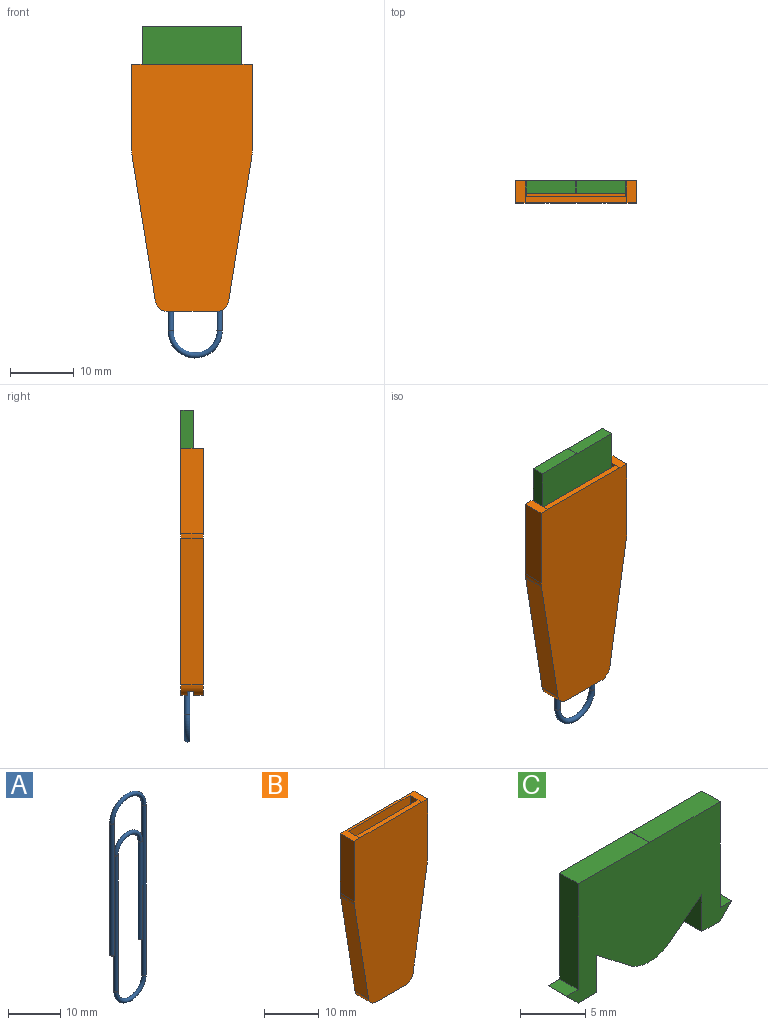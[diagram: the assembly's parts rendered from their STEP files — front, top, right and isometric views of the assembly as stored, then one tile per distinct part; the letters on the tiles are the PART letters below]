
ASSEMBLY  parts=3 mates=2
PART A: 9 faces, bbox 10.3x0.9x49.8 mm
  f0: plane 0.87x0.87mm, normal (0,0,-1), area 0.6mm2, adj f2
  f1: plane 0.87x0.87mm, normal (0,0,-1), area 0.6mm2, adj f8
  f2: cylinder r=0.43mm len=23mm, axis (0,0,1), area 62.9mm2, adj f0,f3
  f3: torus R=3.31mm, axis (0,-1,0), area 28.4mm2, adj f2,f4
  f4: cylinder r=0.43mm len=32mm, axis (0,0,-1), area 87.5mm2, adj f3,f5
  f5: torus R=3.81mm, axis (0,-1,0), area 32.7mm2, adj f4,f6
  f6: cylinder r=0.43mm len=40mm, axis (0,0,1), area 109.3mm2, adj f5,f7
  f7: torus R=4.33mm, axis (0,-1,0), area 37.2mm2, adj f6,f8
  f8: cylinder r=0.43mm len=31mm, axis (0,0,-1), area 84.7mm2, adj f1,f7
PART B: 29 faces, bbox 19x3.5x38.7 mm
  f0: plane 7.55x1.5mm, normal (0,0,-1), area 11.3mm2, adj f15,f16,f25,f26
  f1: plane 15.45x2mm, normal (0,0,1), area 20.4mm2, adj f2,f3,f8,f12,f15,f17,f20,f22
  f2: plane 2x1.51mm, normal (-0.71,0,0.71), area 4.3mm2, adj f1,f5,f20,f22
  f3: plane 2x1.51mm, normal (0.71,0,0.71), area 4.3mm2, adj f1,f6,f20,f22
  f4: plane 9.97x2mm, normal (-1,0,0), area 19.9mm2, adj f5,f11,f20,f22
  f5: plane 2x1.26mm, normal (0,0,-1), area 2.5mm2, adj f2,f4,f20,f22
  f6: plane 2x1.26mm, normal (0,0,-1), area 2.5mm2, adj f3,f7,f20,f22
  f7: plane 9.97x2mm, normal (1,0,0), area 19.9mm2, adj f6,f13,f20,f22
  f8: plane 26.58x1mm, normal (-1,0,0), area 26.6mm2, adj f1,f15,f17,f26
  f9: plane 7.55x1mm, normal (0,0,-1), area 7.5mm2, adj f17,f18,f25,f26
  f10: plane 13.33x3.5mm, normal (1,0,0), area 46.6mm2, adj f11,f16,f18,f27
  f11: plane 3.5x1.51mm, normal (0,0,1), area 5.3mm2, adj f4,f10,f16,f18,f19,f21
  f12: plane 26.58x1mm, normal (1,0,0), area 26.6mm2, adj f1,f15,f17,f25
  f13: plane 3.5x1.51mm, normal (0,0,1), area 5.3mm2, adj f7,f14,f16,f18,f19,f21
  f14: plane 13.33x3.5mm, normal (-1,0,0), area 46.6mm2, adj f13,f16,f18,f28
  f15: plane 27.25x10.54mm, normal (0,1,0), area 286.6mm2, adj f0,f1,f8,f12,f25,f26
  f16: plane 38.72x18.96mm, normal (0,-1,0), area 632.9mm2, adj f0,f10,f11,f13,f14,f19,f23,f24
  f17: plane 27.25x10.54mm, normal (0,-1,0), area 286.6mm2, adj f1,f8,f9,f12,f25,f26
  f18: plane 38.72x18.96mm, normal (0,1,0), area 632.9mm2, adj f9,f10,f11,f13,f14,f21,f23,f24
  f19: plane 15.95x1mm, normal (0,0,1), area 15.9mm2, adj f11,f13,f16,f20
  f20: plane 18.46x11.47mm, normal (0,1,0), area 184.4mm2, adj f1,f2,f3,f4,f5,f6,f7,f19
  f21: plane 15.95x0.5mm, normal (0,0,1), area 8mm2, adj f11,f13,f18,f22
  f22: plane 18.46x11.47mm, normal (0,-1,0), area 184.4mm2, adj f1,f2,f3,f4,f5,f6,f7,f21
  f23: plane 22.92x3.67mm, normal (-0.99,0,-0.16), area 81.3mm2, adj f16,f18,f25,f28
  f24: plane 22.92x3.67mm, normal (0.99,0,-0.16), area 81.3mm2, adj f16,f18,f26,f27
  f25: cylinder r=2mm len=3.5mm, axis (0,1,0), area 8.2mm2, adj f0,f9,f12,f15,f16,f17,f18,f23
  f26: cylinder r=2mm len=3.5mm, axis (0,1,0), area 8.2mm2, adj f0,f8,f9,f15,f16,f17,f18,f24
  f27: cylinder r=5mm len=3.5mm, axis (0,-1,0), area 2.8mm2, adj f10,f16,f18,f24
  f28: cylinder r=5mm len=3.5mm, axis (0,1,0), area 2.8mm2, adj f14,f16,f18,f23
PART C: 21 faces, bbox 18x2x11.2 mm
  f0: cylinder r=3.5mm len=7mm, axis (0,1,0), area 35.3mm2, adj f1,f2,f18,f19,f20
  f1: plane 17.96x11.22mm, normal (0,-1,0), area 158.8mm2, adj f0,f4,f5,f6,f7,f8,f9,f10
  f2: plane 7x7mm, normal (0,1,0), area 38.5mm2, adj f0
  f3: cylinder r=5.72mm len=11.45mm, axis (0,1,0), area 27mm2, adj f11,f12,f17,f19
  f4: plane 7.69x2mm, normal (0,0,1), area 15.4mm2, adj f1,f5,f16,f17
  f5: cylinder r=7.72mm len=2mm, axis (0,1,0), area 0.1mm2, adj f1,f4,f6,f17
  f6: plane 7.72x2mm, normal (0,0,1), area 15.4mm2, adj f1,f5,f7,f17
  f7: plane 9.97x2mm, normal (-1,0,0), area 19.9mm2, adj f1,f6,f8,f17
  f8: plane 2x1.26mm, normal (0,0,1), area 2.5mm2, adj f1,f7,f9,f17
  f9: plane 2x1.26mm, normal (-0.71,0,-0.71), area 3.6mm2, adj f1,f8,f10,f17
  f10: plane 2x2mm, normal (0,0,-1), area 4mm2, adj f1,f9,f11,f17
  f11: plane 3.5x2mm, normal (1,0,0), area 7mm2, adj f1,f3,f10,f17,f18
  f12: plane 3.45x2mm, normal (-1,0,0), area 6.9mm2, adj f1,f3,f13,f17,f20
  f13: plane 2x2mm, normal (0,0,-1), area 4mm2, adj f1,f12,f14,f17
  f14: plane 2x1.26mm, normal (0.71,0,-0.71), area 3.6mm2, adj f1,f13,f15,f17
  f15: plane 2x1.26mm, normal (0,0,1), area 2.5mm2, adj f1,f14,f16,f17
  f16: plane 9.97x2mm, normal (1,0,0), area 19.9mm2, adj f1,f4,f15,f17
  f17: plane 17.96x11.22mm, normal (0,1,0), area 83.4mm2, adj f3,f4,f5,f6,f7,f8,f9,f10
  f18: plane 3.58x2.77mm, normal (-0.61,0,-0.79), area 2.3mm2, adj f0,f1,f11,f19
  f19: plane 11.45x8.51mm, normal (0,1,0), area 37mm2, adj f0,f3,f18,f20
  f20: plane 3.61x2.74mm, normal (0.6,0,-0.8), area 2.3mm2, adj f0,f1,f12,f19
PLACE A t=(4.86,-7.03,67.06)mm
PLACE B rot(axis=(0,1,0),0deg) t=(4.89,-7.53,61.1)mm
PLACE C t=(4.86,-7.03,67.06)mm
MATE slider B.f1 <-> C.f4  axis (0,0,1) through (4.37,-8.03,88.35)mm
MATE fastened A.f7 <-> C.f0  axis (0,-1,0) through (4.34,-7.03,98.06)mm
